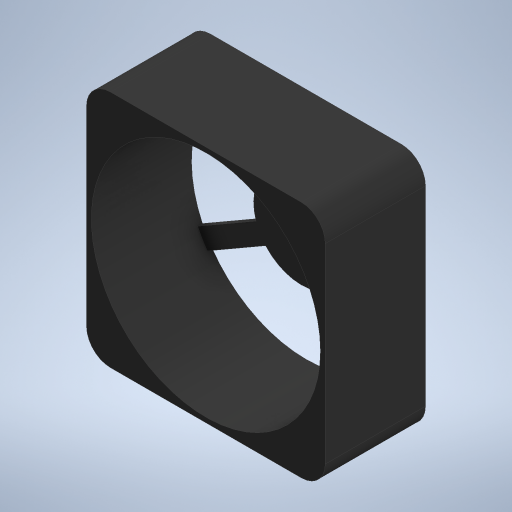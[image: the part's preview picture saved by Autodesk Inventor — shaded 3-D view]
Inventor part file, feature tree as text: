
AUTODESK INVENTOR PART (.ipt)
format: ipt  version: 2023.1 (Build 271208000, 208)  size: 259,072 bytes
history: native  units: mm
features: extrude x3, sketch x3, other x1, fillet x1
ambient origin geometry x8: Origin, YZ Plane, XZ Plane, XY Plane, X Axis, Y Axis, Z Axis, Center Point
bodies: Body1 (feature_tree)
feature tree (8):
  other  "솔리드1"
  extrude  "돌출1"  Depth=25.0mm
  fillet  "모깎기1"  Radius=25.0mm
  extrude  "돌출2"  Depth=10.5mm TaperAngle=0.0deg
  extrude  "돌출3"  Depth=2.5mm
  sketch  "스케치1"
  sketch  "스케치2"
  sketch  "스케치3"
